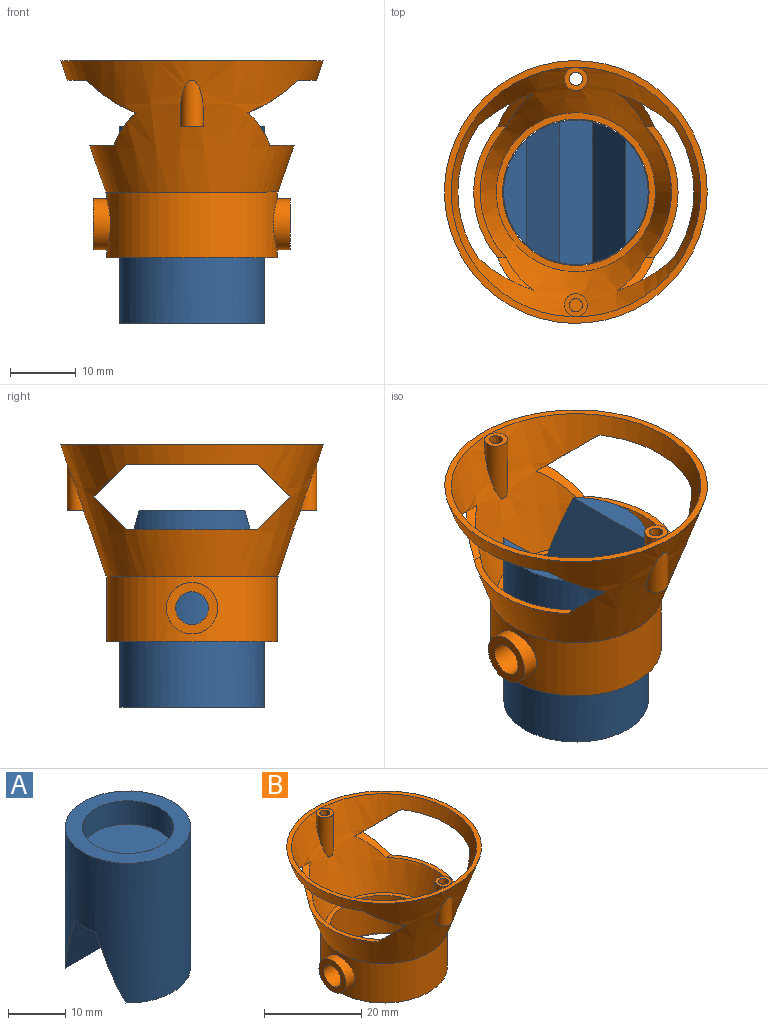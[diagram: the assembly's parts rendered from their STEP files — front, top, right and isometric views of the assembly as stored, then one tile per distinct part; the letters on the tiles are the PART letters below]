
ASSEMBLY  parts=2 mates=1
PART A: 9 faces, bbox 22x22x30 mm
  f0: plane 16.09x3.5mm, normal (0,0,-1), area 38.9mm2, adj f1,f6
  f1: cylinder r=11mm len=30mm, axis (0,0,-1), area 1776.2mm2, adj f0,f2,f3,f4,f5,f6
  f2: plane 22x22mm, normal (0,0,1), area 179.1mm2, adj f1,f7
  f3: plane 16.09x3.5mm, normal (0,0,-1), area 38.9mm2, adj f1,f5
  f4: plane 22x5mm, normal (0,0,-1), area 109mm2, adj f1,f5,f6
  f5: plane 21.42x14.14mm, normal (0,0.94,-0.33), area 289.8mm2, adj f1,f3,f4
  f6: plane 21.42x14.14mm, normal (0,-0.94,-0.33), area 289.8mm2, adj f0,f1,f4
  f7: cylinder r=8mm len=16mm, axis (0,0,1), area 251.3mm2, adj f2,f8
  f8: plane 16x16mm, normal (0,0,1), area 201.1mm2, adj f7
PART B: 45 faces, bbox 40x40x30 mm
  f0: cone r=19mm half-angle=19deg, axis (0,0,1), area 1403.7mm2, adj f8,f10,f18,f19,f20,f21,f22,f23
  f1: cone r=20mm half-angle=19deg, axis (0,0,1), area 1573.1mm2, adj f8,f9,f18,f19,f20,f21,f22,f23
  f2: cylinder r=11.13mm len=7.8mm, axis (0,0,-1), area 28.8mm2, adj f11,f17
  f3: cylinder r=11.13mm len=7.8mm, axis (0,0,-1), area 28.8mm2, adj f4,f16
  f4: cylinder r=3.9mm len=7.8mm, axis (-1,0,0), area 0.4mm2, adj f3,f6
  f5: cylinder r=13mm len=26mm, axis (0,0,1), area 720.1mm2, adj f7,f9,f13,f14
  f6: cylinder r=11.15mm len=22.3mm, axis (0,0,1), area 568.4mm2, adj f4,f10,f11,f44
  f7: plane 26x26mm, normal (0,0,-1), area 104.5mm2, adj f5,f44
  f8: plane 40x40mm, normal (0,0,1), area 122.5mm2, adj f0,f1
  f9: plane 26.23x26.23mm, normal (0,0,-1), area 9.3mm2, adj f1,f5
  f10: plane 24.23x24.23mm, normal (0,0,1), area 70.4mm2, adj f0,f6
  f11: cylinder r=3.9mm len=7.8mm, axis (-1,0,0), area 0.4mm2, adj f2,f6
  f12: plane 7.8x7.8mm, normal (-1,0,0), area 28.2mm2, adj f13,f17
  f13: cylinder r=3.9mm len=7.8mm, axis (-1,0,0), area 56.3mm2, adj f5,f12
  f14: cylinder r=3.9mm len=7.8mm, axis (-1,0,0), area 56.3mm2, adj f5,f15
  f15: plane 7.8x7.8mm, normal (1,0,0), area 28.2mm2, adj f14,f16
  f16: cylinder r=2.5mm len=5mm, axis (-1,0,0), area 62.9mm2, adj f3,f15
  f17: cylinder r=2.5mm len=5mm, axis (-1,0,0), area 62.9mm2, adj f2,f12
  f18: plane 9.72x4.95mm, normal (0,-0.71,-0.71), area 10.5mm2, adj f0,f1,f19,f23
  f19: plane 5.52x4.95mm, normal (0,-0.71,0.71), area 11.7mm2, adj f0,f1,f18,f20
  f20: plane 20x4.98mm, normal (0,0,1), area 21.9mm2, adj f0,f1,f19,f21
  f21: plane 5.52x4.95mm, normal (0,0.71,0.71), area 11.7mm2, adj f0,f1,f20,f22
  f22: plane 9.72x4.95mm, normal (0,0.71,-0.71), area 10.5mm2, adj f0,f1,f21,f23
  f23: plane 20x4.04mm, normal (0,0,-1), area 21.1mm2, adj f0,f1,f18,f22
  f24: plane 20x4.04mm, normal (0,0,-1), area 21.1mm2, adj f0,f1,f25,f29
  f25: plane 9.72x4.95mm, normal (0,0.71,-0.71), area 10.5mm2, adj f0,f1,f24,f26
  f26: plane 5.52x4.95mm, normal (0,0.71,0.71), area 11.7mm2, adj f0,f1,f25,f27
  f27: plane 20x4.98mm, normal (0,0,1), area 21.9mm2, adj f0,f1,f26,f28
  f28: plane 5.52x4.95mm, normal (0,-0.71,0.71), area 11.7mm2, adj f0,f1,f27,f29
  f29: plane 9.72x4.95mm, normal (0,-0.71,-0.71), area 10.5mm2, adj f0,f1,f24,f28
  f30: cylinder r=1mm len=10.97mm, axis (0,0,1), area 63.9mm2, adj f1,f31,f34
  f31: plane 3.5x3.5mm, normal (0,0,1), area 6.5mm2, adj f30,f33
  f32: plane 1x0.08mm, normal (0,0,-1), area 0.1mm2, adj f0,f33
  f33: cylinder r=1.75mm len=10mm, axis (0,0,1), area 55.1mm2, adj f0,f31,f32
  f34: plane 3.5x2.5mm, normal (0,0,-1), area 4.4mm2, adj f1,f30,f35
  f35: cylinder r=1.75mm len=7.03mm, axis (0,0,1), area 30.8mm2, adj f1,f34
  f36: plane 3.5x3.5mm, normal (0,0,1), area 6.5mm2, adj f37,f39
  f37: cylinder r=1mm len=8.06mm, axis (0,0,1), area 32mm2, adj f36,f43
  f38: plane 1x0.08mm, normal (0,0,-1), area 0.1mm2, adj f0,f39
  f39: cylinder r=1.75mm len=10mm, axis (0,0,1), area 55.1mm2, adj f0,f36,f38
  f40: cylinder r=1.75mm len=7.03mm, axis (0,0,1), area 30.8mm2, adj f1,f41
  f41: plane 3.5x2.5mm, normal (0,0,-1), area 4.4mm2, adj f1,f40,f42
  f42: cylinder r=1mm len=4.85mm, axis (0,0,1), area 13.5mm2, adj f1,f41
  f43: cone r=19mm half-angle=19deg, axis (0,0,1), area 9.6mm2, adj f37
  f44: cone r=11.65mm half-angle=45deg, axis (0,0,-1), area 50.6mm2, adj f6,f7
PLACE A rot(axis=(0.71,0.71,0),180deg) t=(27.19,-8.59,39.4)mm
PLACE B t=(27.19,-8.59,29.4)mm
MATE pin_slot A.f1 <-> B.f5  axis (0,0,1) through (27.19,-8.59,24.4)mm
